# Revit family: BDG_BossDesign_PnlPrttns_Qube180
name_source: partatom
category: Furniture
revit_build: Autodesk Revit 2015 (Build: 20140903_1530(x64)
units: mm (PartAtom-declared; Revit-internal decimal feet)

## types (1)
- Qube 180
    Assembly Code = E2020
    AssetType = Movable
    BIMObjectName = BDG_BossDesign_PanelPartitions_Qube180
    Category = Ss_25_10_30 : Framed partition systems
    Color = Silver
    Description = Qube 180
    DurationUnit = year
    ExpectedLife = 5
    Features = Powder coated frame available
    Finish = Manifestations on Glass
    IfcExportAs = IfcFurnishingElementType
    IfcExportType = FRAMED PARTITION SYSTEMS
    Keynote = Ss_25_10_30
    MainColor = Silver
    ManufacturerName = Boss Design
    ManufacturerURL = www.bossdesign.com
    Material = Glass
    Model = Q180
    ModelNumber = Q180
    ModelReference = Qube 180
    NBSDescription = Panel partitions
    NBSReference = 45-35-80/420
    Name = PanelPartitions_Qube180_BossDesign
    NominalHeight = 2220 mm  [stored 7.28346 ft]
    NominalLength = 3021 mm
    NominalWidth = 1598 mm  [stored 5.24278 ft]
    ProductInformation = www.bossdesign.com/product-list/qube-180
    Shape = Semi Circular
    Size = 3021 x 1598 x 2220mm
    URL = www.bossdesign.com
    Uniclass2015Code = Ss_25_10_30
    Uniclass2015Title = Framed partition systems
    Uniclass2015Version = Products v1.10
    Version = 1
    WarrantyDescription = Structural Warranty Excludes Foams and Fabrics
    WarrantyDurationLabor = 5
    WarrantyDurationParts = 5
    WarrantyDurationUnit = year

note: [stored X ft] marks values corroborated as IEEE doubles in the binary element streams (Revit-internal decimal feet)

## geometry (parser evidence)
native form markers: Sweep x2
no freeform markers — native parametric forms only
